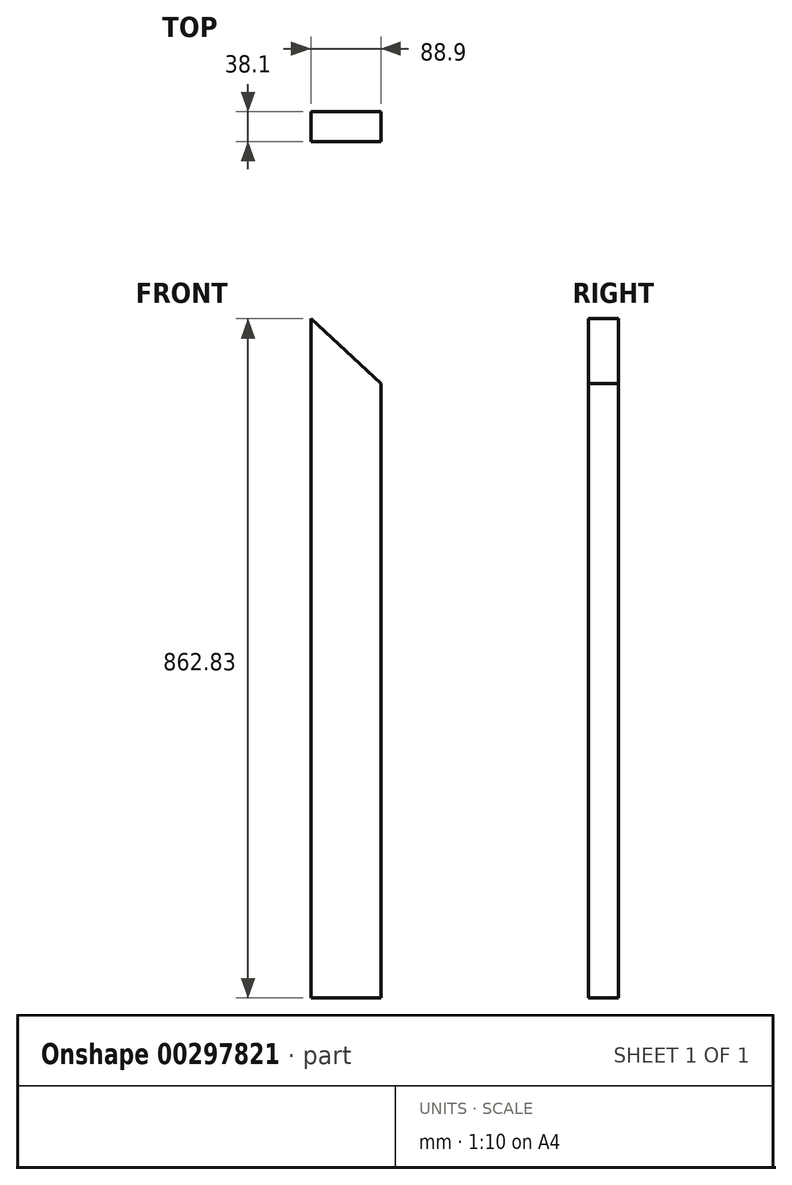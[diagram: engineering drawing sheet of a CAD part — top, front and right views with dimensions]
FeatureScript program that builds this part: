
annotation { "Feature Type Name" : "Feature", "Feature Type Description" : "" }
export const myFeature = defineFeature(function(context is Context, id is Id, definition is map)
    precondition{}
    {
        {
            var Q0;
            Q0=qCreatedBy(makeId("Top.planeOp"),FACE);
            var sketch = newSketch(context, id + "F0", { "sketchPlane" : qUnion([Q0])});
            skLineSegment(sketch, "E0.bottom", {"start": v(0, 0) * mm, "end": v(88.9, 0) * mm});
            skLineSegment(sketch, "E0.top", {"start": v(0, 38.1) * mm, "end": v(88.9, 38.1) * mm});
            skLineSegment(sketch, "E0.left", {"start": v(0, 0) * mm, "end": v(0, 38.1) * mm});
            skLineSegment(sketch, "E0.right", {"start": v(88.9, 0) * mm, "end": v(88.9, 38.1) * mm});
            skSolve(sketch);
        }
        {
            var Q0;
            Q0=makeQuery(id+"F0.imprint","IMPRINT",FACE,{"disambiguationData":[TD([[makeQuery(id+"F0.imprint","IMPRINT",EDGE,{"derivedFrom":sQuery(id+"F0.wireOp",EDGE,"E0.bottom")}),1.0]])]});
            extrude(context, id + "F1", {"entities" : qUnion([Q0]), "depth" : 901.7 * mm});
        }
        {
            var Q0;
            Q0=makeQuery(id+"F1.opExtrude","SWEPT_FACE",FACE,{"disambiguationData":[OSD([sQuery(id+"F0.wireOp",EDGE,"E0.bottom")])]});
            var sketch = newSketch(context, id + "F2", { "sketchPlane" : qUnion([Q0])});
            skLineSegment(sketch, "E1", {"start": v(0, 901.7) * mm, "end": v(0, 983.93) * mm});
            skLineSegment(sketch, "E2", {"start": v(0, 983.93) * mm, "end": v(88.9, 901.7) * mm});
            skLineSegment(sketch, "E3", {"start": v(88.9, 901.7) * mm, "end": v(0, 901.7) * mm});
            skLineSegment(sketch, "E4", {"start": v(0, 983.93) * mm, "end": v(0, 862.83) * mm});
            skLineSegment(sketch, "E5", {"start": v(88.9, 901.7) * mm, "end": v(88.9, 780.6) * mm});
            skLineSegment(sketch, "E6", {"start": v(0, 862.83) * mm, "end": v(88.9, 780.6) * mm});
            skSolve(sketch);
        }
        {
            var Q0;
            Q0=makeQuery(id+"F2.imprint","IMPRINT",FACE,{"disambiguationData":[TD([[makeQuery(id+"F2.imprint","IMPRINT",EDGE,{"derivedFrom":sQuery(id+"F2.wireOp",EDGE,"E1")}),-1.0]])]});
            var Q1;
            {var subQ0=sQuery(id+"F2.wireOp",EDGE,"E3");Q1=makeQuery(id+"F2.imprint","IMPRINT",FACE,{"disambiguationData":[TD([[makeQuery(id+"F2.imprint","IMPRINT",EDGE,{"derivedFrom":subQ0}),-1.0]])]});}
            extrude(context, id + "F3", {"entities" : qUnion([Q0, Q1]), "operationType" : NewBodyOperationType.REMOVE, "oppositeDirection" : true, "depth" : 38.1 * mm});
        }
    });
